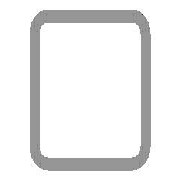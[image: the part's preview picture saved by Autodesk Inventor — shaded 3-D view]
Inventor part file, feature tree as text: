
AUTODESK INVENTOR PART (.ipt)
format: ipt  version: 2021 (Build 250183000, 183)  size: 128,000 bytes
history: native  units: mm (DEFAULTED — no unit token found)
features: other x3, sketch x3, extrude x1, plane x1
ambient origin geometry x8: Origin, YZ Plane, XZ Plane, XY Plane, X Axis, Y Axis, Z Axis, Center Point
bodies: Solid1 (feature_tree)
feature tree (8):
  other  "Driven Length"
  other  "Płaszczyzna początkowa"
  other  "Płaszczyzna końcowa"
  extrude  "Bryła"  TaperAngle=0.0deg  [1 undecoded]
  sketch  "Szkic"
  sketch  "Sketch3"  dims[d3=2000.0mm d4=0.0mm]
  plane  "Work Plane3"
  sketch  "Sketch4"  dims[d7=5.0mm d9=25.0mm d11=25.0mm d12=2.5mm d13=-0.0mm d14=2000.0mm d15=12.5mm d16=12.5mm d17=90.0deg d18=2000.0mm]
note: 1 required parameter value undecoded (feature->parameter linkage not recoverable at this tier; creation-order binding heuristic only, values carry confidence <= 0.55)
